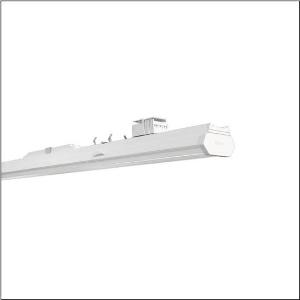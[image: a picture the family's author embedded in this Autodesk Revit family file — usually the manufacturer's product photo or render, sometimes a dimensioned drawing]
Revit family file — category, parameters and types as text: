
# Revit family: licross_11_protected_tw_51td1btnt8xx
name_source: partatom
category: Lighting Fixtures
units: mm (PartAtom-declared; Revit-internal decimal feet)

## family parameters
Cut with Voids When Loaded = No
Host = Face
Light Source = No
Part Type = Normal
Room Calculation Point = No
Round Connector Dimension = Use Diameter
Shared = No

## types (1)
- --- (1 x LED 2700 K ... 6500 K, 8450 lm, 56 W, 2700K)
    Apparent Load = 56 VA
    CIE Flux Codes = 54 82 95 97 100
    Color Rendering = 80
    Color Temperature = 2700K
    Default Elevation = 1800 mm
    Description = Licross 11 Protected TW, luminaire insert, of sheet steel, galvanised, coil coated, white, length: 1.500mm, width: 90mm, height: 101mm, LED rated luminous flux: 8.450lm, light colour: 8tw, SDCM (Standard Deviation of Colour Matching)MacAdam ≤ 2 SDCM (initial), control gear: DALI DT8, with plug, 5-pole, with phase selection, mains connection: 220..240V, AC, 50/60Hz, rated input power: 56W, internal wiring halogen-free, primary optical cover: cover, of PMMA, light emission: direct distribution, primary light characteristic: symmetric, protection rating (complete): IP54, insulation class (complete): insulation class I (protective earthing), certification: CE, ENEC, VDE, UKCA, protection symbol: D if used in an environment with non-conductive dust loads with corresponding accessories, impact resistance: IK06, permissible ambient temperature for indoor applications: -25..+35°C, corresponds to IFS (International Featured Standards) requirements for safety and quality in the food industry, reducing of maximum allowable ambient temperature of 5°C with ceiling mounting, LABS conformity tested according to VDMA 24364:2018-05, The light source and the operating device comply with the requirements of the Ecodesign Regulation (EU) 2019/2020 and are replaceable in accordance with this regulation, packaging unit: 1 piece
    Height = 92 mm
    Lamp = 1 x LED 2700 K ... 6500 K
    Lamp Light Flux = 8450 lm
    Lamp Power = 56 W
    Lamp count = 1
    Length = 1500 mm
    Luminous efficacy = 151 lm/W
    Manufacturer = Siteco
    ModVariant = No
    Model = 51TD1BTNT8XX
    Mounting Place = Ceiling
    Mounting Type = Pendant
    Number of Poles = 1
    OnlyDefault = Yes
    Power Factor = 1
    Product Name = Licross 11 Protected TW
    Product group = luminaire insert | ceiling pendant
    ProductGroupID = 901
    Protection Class = Protection class I
    Protection Degree = IP 54
    RLX_Detail_Level = 1
    RLX_Emergency_Light_Flux = 0 lm
    RLX_Emergency_Type = 0
    RLX_Emergency_Type_DB = No
    RlxData = <blob elided: 20949 chars, md5=b2cf1153>
    Socket = socket
    Standby Power = 0 W
    System Light Flux = 8450 lm
    System Power = 56 W
    Type Comments = individual setting: CCT=2700K
    Type Image = l_1256145.jpg
    URL = http://relux.com
    VarID = @adj_057765
    Voltage = 0 V
    Weight = 0.00 kg
    Width = 88 mm

## geometry (parser evidence)
native form markers: Blend x4, Sweep x10
no freeform markers — native parametric forms only
